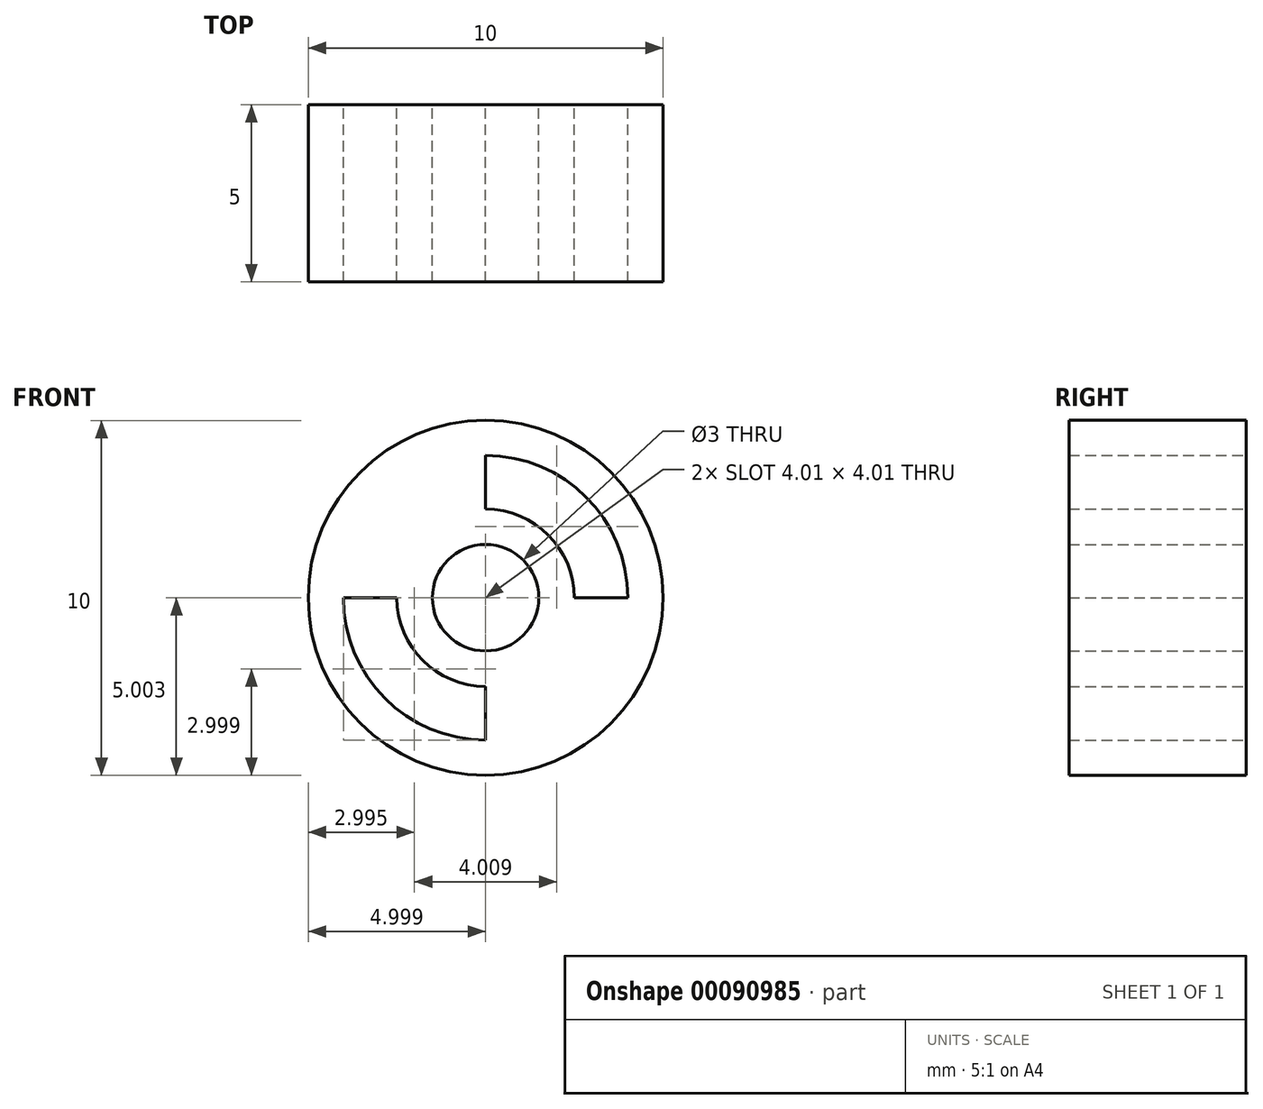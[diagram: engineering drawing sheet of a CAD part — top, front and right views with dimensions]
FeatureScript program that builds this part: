
annotation { "Feature Type Name" : "Feature", "Feature Type Description" : "" }
export const myFeature = defineFeature(function(context is Context, id is Id, definition is map)
    precondition{}
    {
        {
            var Q0;
            Q0=qCreatedBy(makeId("Front.planeOp"),FACE);
            var sketch = newSketch(context, id + "F0", { "sketchPlane" : qUnion([Q0])});
            skCircle(sketch, "E0", {"center": v(7.04, 1.61) * mm, "radius": 5 * mm});
            skCircle(sketch, "E1", {"center": v(7.04, 1.61) * mm, "radius": 1.5 * mm});
            skArc(sketch, "E2.0", {"start": v(4.54, 1.61) * mm, "mid": v(5.27, -0.15) * mm, "end": v(7.04, -0.89) * mm});
            skArc(sketch, "E3.0", {"start": v(3.03, 1.61) * mm, "mid": v(4.2, -1.22) * mm, "end": v(7.04, -2.4) * mm});
            skLineSegment(sketch, "E4", {"start": v(7.04, 4.11) * mm, "end": v(7.04, 5.62) * mm});
            skLineSegment(sketch, "E5", {"start": v(9.54, 1.61) * mm, "end": v(11.05, 1.61) * mm});
            skLineSegment(sketch, "E6", {"start": v(7.04, -0.89) * mm, "end": v(7.04, -2.4) * mm});
            skLineSegment(sketch, "E7", {"start": v(4.54, 1.61) * mm, "end": v(3.03, 1.61) * mm});
            skArc(sketch, "E8.trimOffspring", {"start": v(9.54, 1.61) * mm, "mid": v(8.8, 3.38) * mm, "end": v(7.04, 4.11) * mm});
            skArc(sketch, "E9.trimOffspring", {"start": v(11.05, 1.61) * mm, "mid": v(9.87, 4.45) * mm, "end": v(7.04, 5.62) * mm});
            skSolve(sketch);
        }
        {
            var Q0;
            Q0=makeQuery(id+"F0.imprint","IMPRINT",FACE,{"disambiguationData":[TD([[makeQuery(id+"F0.imprint","IMPRINT",EDGE,{"derivedFrom":sQuery(id+"F0.wireOp",EDGE,"E0")}),1.0]])]});
            extrude(context, id + "F1", {"entities" : qUnion([Q0]), "depth" : 5 * mm});
        }
    });
